# Revit family: F112-36x18x18
name_source: partatom
category: Furniture Systems
units: mm (PartAtom-declared; Revit-internal decimal feet)

## family parameters
Always vertical = Yes
Cut with Voids When Loaded = No
Part Type = Normal
Room Calculation Point = No
Round Connector Dimension = Use Diameter
Shared = No
Work Plane-Based = No

## types (4) — shared parameters
3" Rectangle Leg = <By Category>
Base = <By Category>
Description = Network Series - Diamond Ottoman (Seat height 18")
Glide = <By Category>
Laminate Top = <By Category>
Leg H = 0' - 1 1/2"
Low Profile = Black
Manufacturer = FOMCORE
Model = F112-36x18x18
Seat Fabric = <By Category>
Side Fabric = <By Category>
URL = https://fomcore.com

## per-type parameters (varying)
| type | G1 | L- TOP | L1 | LEG OPTIONS | Seat H |
| F112-36x18x18-G1 | Yes | No | No | 1 | 1' - 6" |
| F112-36x18x18-G1-TFL | Yes | Yes | No | 1 | 1' - 5 1/4" |
| F112-36x18x18-L1 | No | No | Yes | 2 | 1' - 6" |
| F112-36x18x18-L1-TFL | No | Yes | Yes | 2 | 1' - 5 1/4" |

## geometry (parser evidence)
native form markers: Sweep x2
no freeform markers — native parametric forms only
